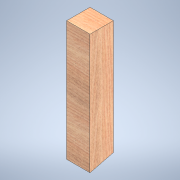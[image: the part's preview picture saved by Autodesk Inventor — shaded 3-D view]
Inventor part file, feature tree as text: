
AUTODESK INVENTOR PART (.ipt)
format: ipt  version: 2020.2 (Build 242310000, 310)  size: 119,808 bytes
history: native  units: in
note: dims shown in document units (in); Inventor stores cm internally (conversion verified against a paired STEP export)
features: extrude x1, sketch x1
ambient origin geometry x8: Origin, YZ Plane, XZ Plane, XY Plane, X Axis, Y Axis, Z Axis, Center Point
bodies: Solid1 (feature_tree)
feature tree (2):
  extrude  "Extrusion1"  TaperAngle=0.0deg  [1 undecoded]
  sketch  "Sketch1"  dims[d3=3.5in d4=0.0in]
note: 1 required parameter value undecoded (feature->parameter linkage not recoverable at this tier; creation-order binding heuristic only, values carry confidence <= 0.55)
